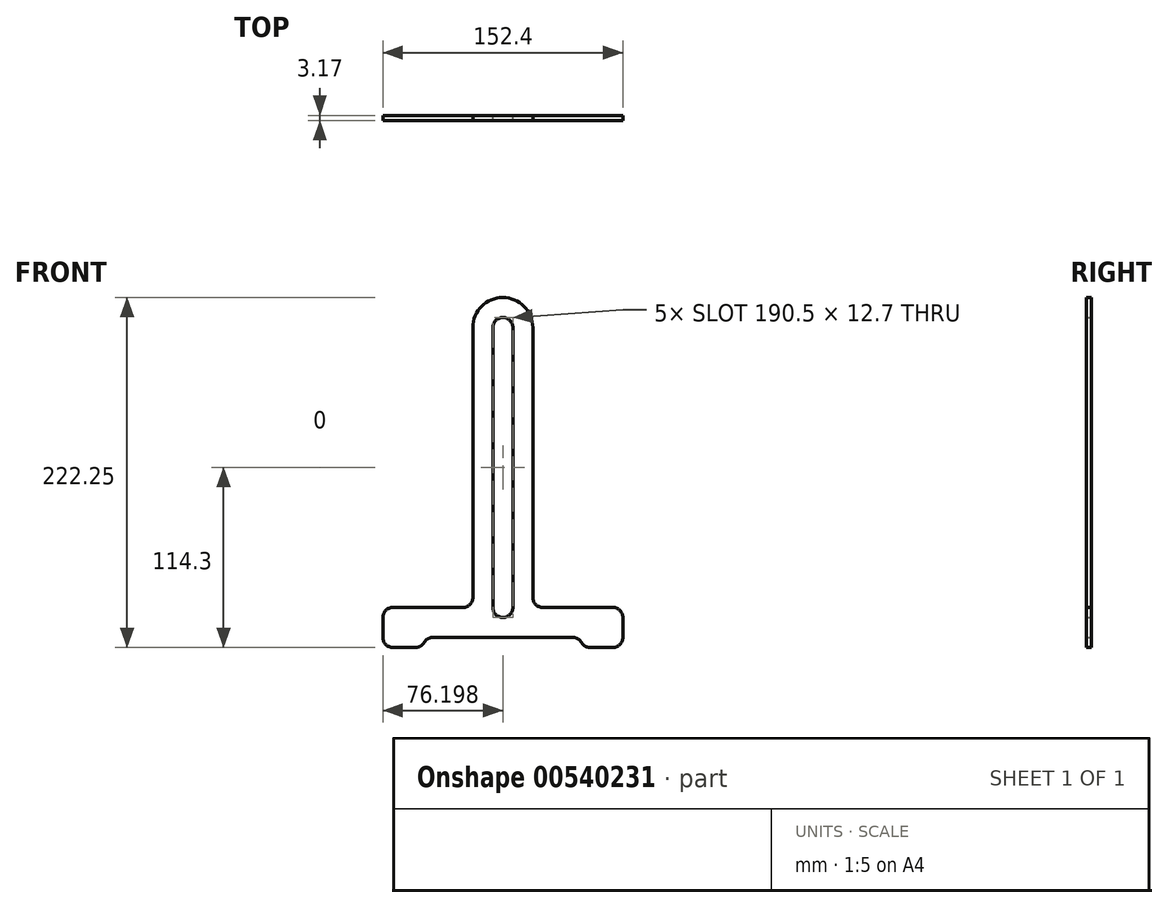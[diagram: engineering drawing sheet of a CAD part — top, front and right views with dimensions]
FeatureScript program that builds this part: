
annotation { "Feature Type Name" : "Feature", "Feature Type Description" : "" }
export const myFeature = defineFeature(function(context is Context, id is Id, definition is map)
    precondition{}
    {
        {
            var Q0;
            Q0=qCreatedBy(makeId("Front.planeOp"),FACE);
            var sketch = newSketch(context, id + "F0", { "sketchPlane" : qUnion([Q0])});
            skLineSegment(sketch, "E0", {"start": v(-96.85, 203.2) * mm, "end": v(-96.85, 31.75) * mm});
            skLineSegment(sketch, "E1", {"start": v(-103.2, 25.4) * mm, "end": v(-147.65, 25.4) * mm});
            skLineSegment(sketch, "E2", {"start": v(-154, 19.05) * mm, "end": v(-154, 6.35) * mm});
            skLineSegment(sketch, "E3", {"start": v(-147.65, 0) * mm, "end": v(-133.25, 0) * mm});
            skLineSegment(sketch, "E4", {"start": v(-1.6, 6.35) * mm, "end": v(-1.6, 19.05) * mm});
            skLineSegment(sketch, "E5", {"start": v(-7.95, 25.4) * mm, "end": v(-52.4, 25.4) * mm});
            skLineSegment(sketch, "E6", {"start": v(-58.75, 31.75) * mm, "end": v(-58.75, 203.2) * mm});
            skArc(sketch, "E7", {"start": v(-58.75, 203.2) * mm, "mid": v(-77.8, 222.25) * mm, "end": v(-96.85, 203.2) * mm});
            skLineSegment(sketch, "E8", {"start": v(-77.8, 203.2) * mm, "end": v(-77.8, 0) * mm, "construction": true});
            skLineSegment(sketch, "E9", {"start": v(-84.15, 203.2) * mm, "end": v(-84.15, 25.4) * mm});
            skLineSegment(sketch, "E10", {"start": v(-71.45, 203.2) * mm, "end": v(-71.45, 25.4) * mm});
            skArc(sketch, "E11", {"start": v(-71.45, 203.2) * mm, "mid": v(-77.8, 209.55) * mm, "end": v(-84.15, 203.2) * mm});
            skArc(sketch, "E12", {"start": v(-84.15, 25.4) * mm, "mid": v(-77.8, 19.05) * mm, "end": v(-71.45, 25.4) * mm});
            skPoint(sketch, "E13.visualSharp", {"position": v(-154, 25.4) * mm});
            skArc(sketch, "E13.filletArc", {"start": v(-147.65, 25.4) * mm, "mid": v(-152.14, 23.54) * mm, "end": v(-154, 19.05) * mm});
            skPoint(sketch, "E14.visualSharp", {"position": v(-154, 0) * mm});
            skArc(sketch, "E14.filletArc", {"start": v(-154, 6.35) * mm, "mid": v(-152.14, 1.86) * mm, "end": v(-147.65, 0) * mm});
            skPoint(sketch, "E15.visualSharp", {"position": v(-1.6, 25.4) * mm});
            skArc(sketch, "E15.filletArc", {"start": v(-1.6, 19.05) * mm, "mid": v(-3.46, 23.54) * mm, "end": v(-7.95, 25.4) * mm});
            skPoint(sketch, "E16.visualSharp", {"position": v(-1.6, 0) * mm});
            skArc(sketch, "E16.filletArc", {"start": v(-7.95, 0) * mm, "mid": v(-3.46, 1.86) * mm, "end": v(-1.6, 6.35) * mm});
            skPoint(sketch, "E17.visualSharp", {"position": v(-58.75, 25.4) * mm});
            skArc(sketch, "E17.filletArc", {"start": v(-58.75, 31.75) * mm, "mid": v(-56.9, 27.26) * mm, "end": v(-52.4, 25.4) * mm});
            skPoint(sketch, "E18.visualSharp", {"position": v(-96.85, 25.4) * mm});
            skArc(sketch, "E18.filletArc", {"start": v(-103.2, 25.4) * mm, "mid": v(-98.71, 27.26) * mm, "end": v(-96.85, 31.75) * mm});
            skLineSegment(sketch, "E19", {"start": v(-122.25, 6.35) * mm, "end": v(-33.35, 6.35) * mm});
            skArc(sketch, "E20", {"start": v(-122.25, 6.35) * mm, "mid": v(-125.43, 5.5) * mm, "end": v(-127.75, 3.17) * mm});
            skArc(sketch, "E21", {"start": v(-33.35, 6.35) * mm, "mid": v(-30.18, 5.5) * mm, "end": v(-27.85, 3.17) * mm});
            skPoint(sketch, "E22.orphan", {"position": v(-242.53, 0) * mm});
            skPoint(sketch, "E23", {"position": v(-77.8, 0) * mm});
            skLineSegment(sketch, "E24.trimOffspring", {"start": v(-22.35, 0) * mm, "end": v(-7.95, 0) * mm});
            skPoint(sketch, "E25.visualSharp", {"position": v(-128.6, 0) * mm});
            skArc(sketch, "E25.filletArc", {"start": v(-133.25, 0) * mm, "mid": v(-130.08, 0.85) * mm, "end": v(-127.75, 3.17) * mm});
            skPoint(sketch, "E26.visualSharp", {"position": v(-27, 0) * mm});
            skArc(sketch, "E26.filletArc", {"start": v(-27.85, 3.17) * mm, "mid": v(-25.53, 0.85) * mm, "end": v(-22.35, 0) * mm});
            skSolve(sketch);
        }
        {
            var Q0;
            Q0=makeQuery(id+"F0.imprint","IMPRINT",FACE,{"disambiguationData":[TD([[makeQuery(id+"F0.imprint","IMPRINT",EDGE,{"derivedFrom":sQuery(id+"F0.wireOp",EDGE,"E0")}),1.0]])]});
            extrude(context, id + "F1", {"entities" : qUnion([Q0]), "depth" : 3.17 * mm, "offsetDistance" : 25.4 * mm});
        }
    });
